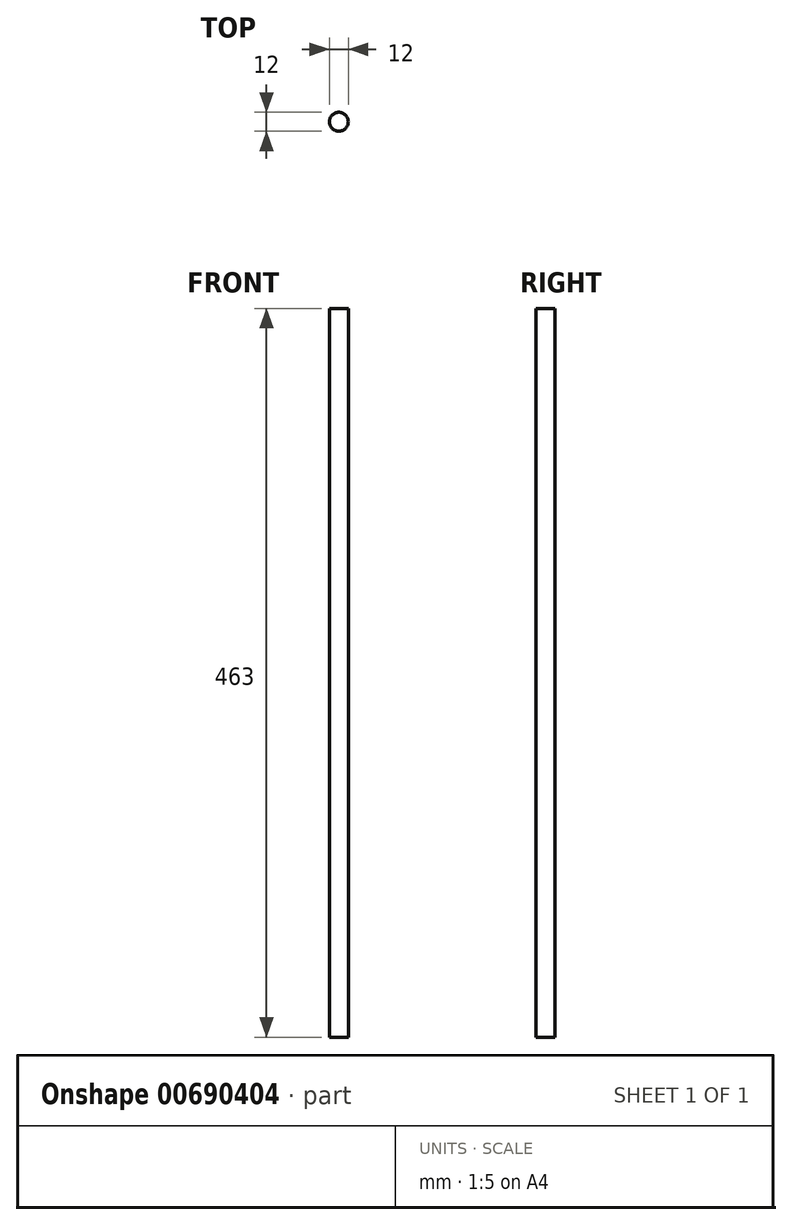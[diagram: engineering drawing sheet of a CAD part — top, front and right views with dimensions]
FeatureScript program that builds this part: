
annotation { "Feature Type Name" : "Feature", "Feature Type Description" : "" }
export const myFeature = defineFeature(function(context is Context, id is Id, definition is map)
    precondition{}
    {
        {
            var Q0;
            Q0=qCreatedBy(makeId("Top.planeOp"),FACE);
            var sketch = newSketch(context, id + "F0", { "sketchPlane" : qUnion([Q0])});
            skCircle(sketch, "E0", {"center": v(0, 0) * mm, "radius": 6 * mm});
            skSolve(sketch);
        }
        {
            var Q0;
            Q0 = qSketchRegion(id + "F0", true);
            extrude(context, id + "F1", {"entities" : qUnion([Q0]), "depth" : 463 * mm, "offsetDistance" : 25 * mm});
        }
    });
